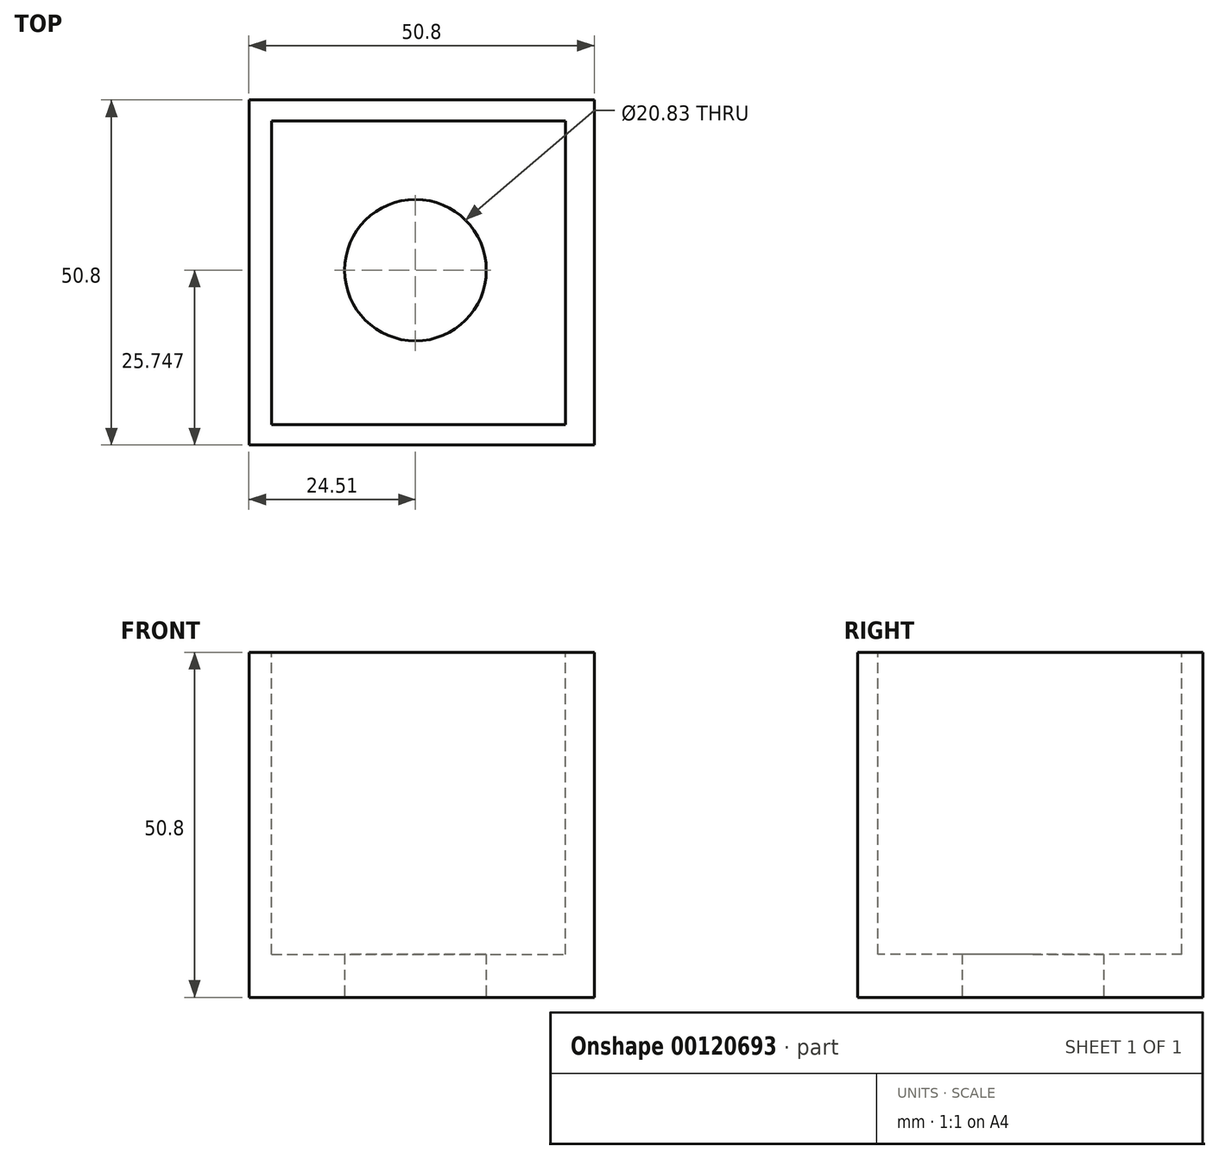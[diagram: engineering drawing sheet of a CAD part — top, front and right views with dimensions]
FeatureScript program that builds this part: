
annotation { "Feature Type Name" : "Feature", "Feature Type Description" : "" }
export const myFeature = defineFeature(function(context is Context, id is Id, definition is map)
    precondition{}
    {
        {
            var Q0;
            Q0=qCreatedBy(makeId("Top.planeOp"),FACE);
            var sketch = newSketch(context, id + "F0", { "sketchPlane" : qUnion([Q0])});
            skLineSegment(sketch, "E0.bottom", {"start": v(-24.5, 35.44) * mm, "end": v(26.3, 35.44) * mm});
            skLineSegment(sketch, "E0.top", {"start": v(-24.5, -15.36) * mm, "end": v(26.3, -15.36) * mm});
            skLineSegment(sketch, "E0.left", {"start": v(-24.5, 35.44) * mm, "end": v(-24.5, -15.36) * mm});
            skLineSegment(sketch, "E0.right", {"start": v(26.3, 35.44) * mm, "end": v(26.3, -15.36) * mm});
            skSolve(sketch);
        }
        {
            var Q0;
            Q0 = qSketchRegion(id + "F0", true);
            extrude(context, id + "F1", {"entities" : qUnion([Q0]), "depth" : 50.8 * mm});
        }
        {
            var Q0;
            Q0=makeQuery(id+"F1.opExtrude","CAP_FACE",FACE,{"disambiguationData":[OSD([sQuery(id+"F0.wireOp",EDGE,"E0.bottom"),sQuery(id+"F0.wireOp",EDGE,"E0.top"),sQuery(id+"F0.wireOp",EDGE,"E0.left"),sQuery(id+"F0.wireOp",EDGE,"E0.right")])],"isStart":false});
            var sketch = newSketch(context, id + "F2", { "sketchPlane" : qUnion([Q0])});
            skLineSegment(sketch, "E1.bottom", {"start": v(-21.16, 32.33) * mm, "end": v(22.05, 32.33) * mm});
            skLineSegment(sketch, "E1.top", {"start": v(-21.16, -12.37) * mm, "end": v(22.05, -12.37) * mm});
            skLineSegment(sketch, "E1.left", {"start": v(-21.16, 32.33) * mm, "end": v(-21.16, -12.37) * mm});
            skLineSegment(sketch, "E1.right", {"start": v(22.05, 32.33) * mm, "end": v(22.05, -12.37) * mm});
            skSolve(sketch);
        }
        {
            var Q0;
            Q0=makeQuery(id+"F2.imprint","IMPRINT",FACE,{"disambiguationData":[TD([[makeQuery(id+"F2.imprint","IMPRINT",EDGE,{"derivedFrom":sQuery(id+"F2.wireOp",EDGE,"E1.bottom")}),-1.0]])]});
            extrude(context, id + "F3", {"entities" : qUnion([Q0]), "operationType" : NewBodyOperationType.REMOVE, "oppositeDirection" : true, "depth" : 44.45 * mm});
        }
        {
            var Q0;
            Q0=makeQuery(id+"F1.opExtrude","CAP_FACE",FACE,{"disambiguationData":[OSD([sQuery(id+"F0.wireOp",EDGE,"E0.bottom"),sQuery(id+"F0.wireOp",EDGE,"E0.top"),sQuery(id+"F0.wireOp",EDGE,"E0.left"),sQuery(id+"F0.wireOp",EDGE,"E0.right")])],"isStart":true});
            var sketch = newSketch(context, id + "F4", { "sketchPlane" : qUnion([Q0])});
            skLineSegment(sketch, "E2", {"start": v(-24.5, 12.96) * mm, "end": v(26.3, -35.44) * mm, "construction": true});
            skCircle(sketch, "E3", {"center": v(0, -10.39) * mm, "radius": 10.41 * mm});
            skSolve(sketch);
        }
        {
            var Q0;
            Q0 = qSketchRegion(id + "F4", true);
            extrude(context, id + "F5", {"entities" : qUnion([Q0]), "operationType" : NewBodyOperationType.REMOVE, "endBound" : BoundingType.THROUGH_ALL, "oppositeDirection" : true, "depth" : 25.4 * mm});
        }
    });
